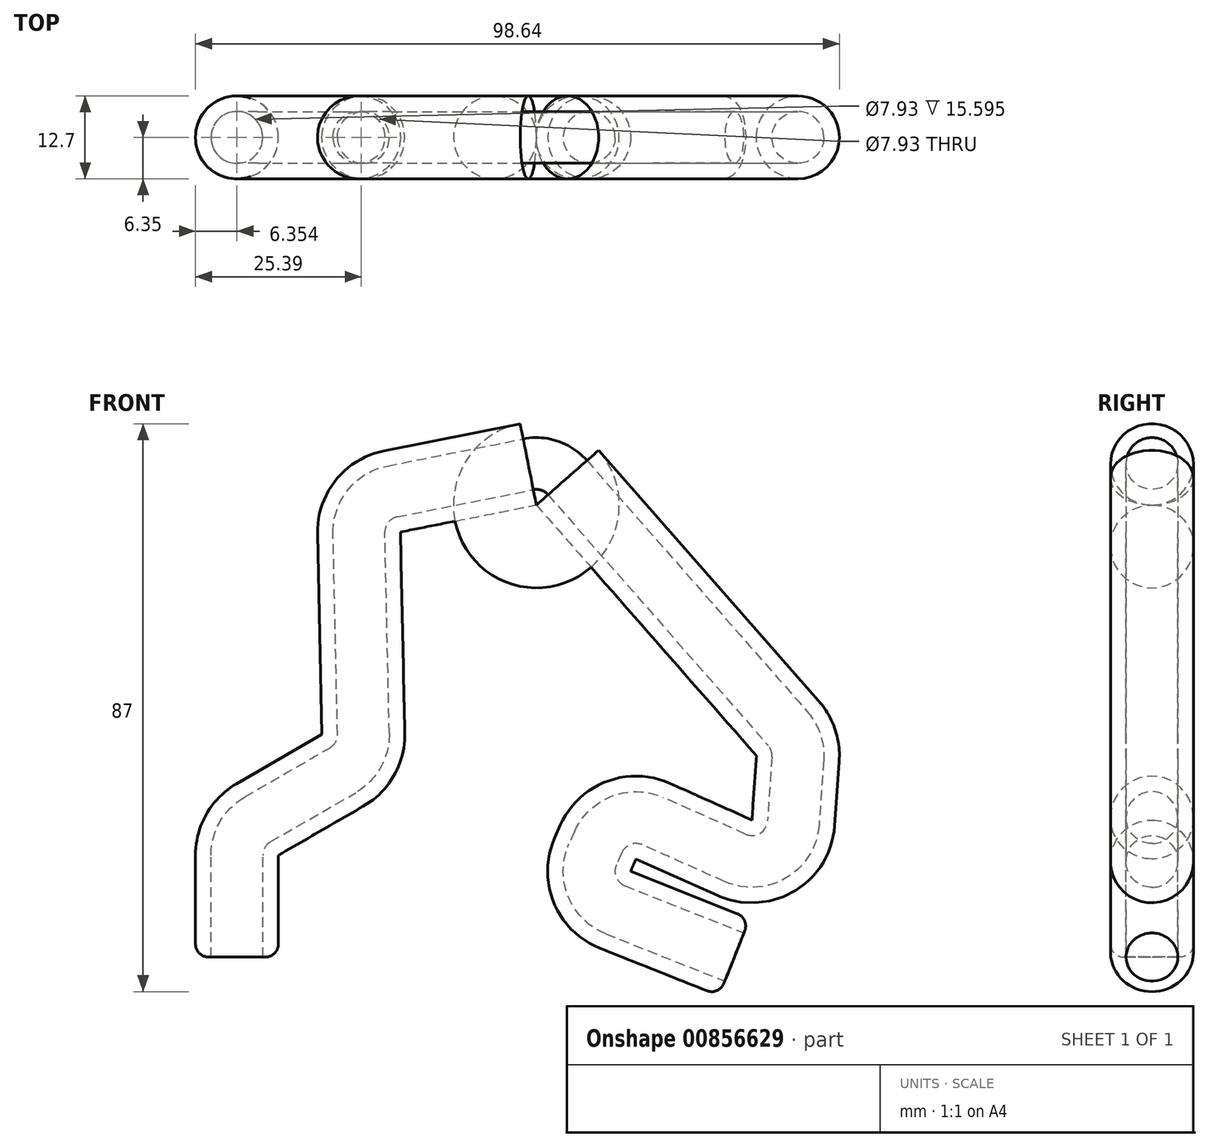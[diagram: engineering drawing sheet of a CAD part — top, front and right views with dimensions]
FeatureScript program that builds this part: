
annotation { "Feature Type Name" : "Feature", "Feature Type Description" : "" }
export const myFeature = defineFeature(function(context is Context, id is Id, definition is map)
    precondition{}
    {
        {
            var Q0;
            Q0=qCreatedBy(makeId("Front.planeOp"),FACE);
            var sketch = newSketch(context, id + "F0", { "sketchPlane" : qUnion([Q0])});
            skLineSegment(sketch, "E0", {"start": v(-44.89, 0) * mm, "end": v(-44.89, 15.6) * mm});
            skLineSegment(sketch, "E1", {"start": v(-41.71, 21.1) * mm, "end": v(-28.68, 28.62) * mm});
            skLineSegment(sketch, "E2", {"start": v(-25.5, 34.26) * mm, "end": v(-26.2, 64.96) * mm});
            skLineSegment(sketch, "E3", {"start": v(-21.08, 71.33) * mm, "end": v(-0.26, 75.48) * mm});
            skLineSegment(sketch, "E4", {"start": v(5.76, 73.44) * mm, "end": v(39.48, 35.03) * mm});
            skLineSegment(sketch, "E5", {"start": v(41.04, 30.39) * mm, "end": v(40.34, 20.56) * mm});
            skLineSegment(sketch, "E6", {"start": v(31.42, 15.2) * mm, "end": v(18.83, 20.82) * mm});
            skLineSegment(sketch, "E7", {"start": v(10.45, 17.61) * mm, "end": v(9.61, 15.75) * mm});
            skLineSegment(sketch, "E8", {"start": v(13.07, 7.26) * mm, "end": v(31.31, 0) * mm});
            skPoint(sketch, "E9.visualSharp", {"position": v(-44.89, 19.26) * mm});
            skArc(sketch, "E9.filletArc", {"start": v(-41.71, 21.1) * mm, "mid": v(-44.04, 18.77) * mm, "end": v(-44.89, 15.6) * mm});
            skPoint(sketch, "E10.visualSharp", {"position": v(-25.43, 30.5) * mm});
            skArc(sketch, "E10.filletArc", {"start": v(-28.68, 28.62) * mm, "mid": v(-26.32, 31) * mm, "end": v(-25.5, 34.26) * mm});
            skPoint(sketch, "E11.visualSharp", {"position": v(-26.3, 70.3) * mm});
            skArc(sketch, "E11.filletArc", {"start": v(-21.08, 71.33) * mm, "mid": v(-24.8, 69.08) * mm, "end": v(-26.2, 64.96) * mm});
            skPoint(sketch, "E12.visualSharp", {"position": v(3.34, 76.2) * mm});
            skArc(sketch, "E12.filletArc", {"start": v(5.76, 73.44) * mm, "mid": v(3.02, 75.27) * mm, "end": v(-0.26, 75.48) * mm});
            skPoint(sketch, "E13.visualSharp", {"position": v(41.23, 33.03) * mm});
            skArc(sketch, "E13.filletArc", {"start": v(41.04, 30.39) * mm, "mid": v(40.72, 32.86) * mm, "end": v(39.48, 35.03) * mm});
            skPoint(sketch, "E14.visualSharp", {"position": v(39.7, 11.5) * mm});
            skArc(sketch, "E14.filletArc", {"start": v(31.42, 15.2) * mm, "mid": v(37.27, 15.56) * mm, "end": v(40.34, 20.56) * mm});
            skPoint(sketch, "E15.visualSharp", {"position": v(13.03, 23.41) * mm});
            skArc(sketch, "E15.filletArc", {"start": v(18.83, 20.82) * mm, "mid": v(13.98, 20.96) * mm, "end": v(10.45, 17.61) * mm});
            skPoint(sketch, "E16.visualSharp", {"position": v(6.92, 9.7) * mm});
            skArc(sketch, "E16.filletArc", {"start": v(9.61, 15.75) * mm, "mid": v(9.53, 10.77) * mm, "end": v(13.07, 7.26) * mm});
            skSolve(sketch);
        }
        {
            var Q0;
            Q0=qCreatedBy(makeId("Top.planeOp"),FACE);
            var sketch = newSketch(context, id + "F1", { "sketchPlane" : qUnion([Q0])});
            skCircle(sketch, "E17", {"center": v(-44.89, 0) * mm, "radius": 6.35 * mm});
            skSolve(sketch);
        }
        {
            var Q0;
            Q0=makeQuery(id+"F1.imprint","IMPRINT",FACE,{"disambiguationData":[TD([[makeQuery(id+"F1.imprint","IMPRINT",EDGE,{"derivedFrom":sQuery(id+"F1.wireOp",EDGE,"E17")}),1.0]])]});
            var Q1;
            Q1 = qConstructionFilter(qBodyType(qCreatedBy(id + "F0" ,EDGE), BodyType.WIRE), ConstructionObject.NO);
            sweep(context, id + "F2", {"profiles" : qUnion([Q0]), "path" : qUnion([Q1])});
        }
        {
            var Q0;
            Q0=makeQuery(id+"F2.opSweep","CAP_FACE",FACE,{"disambiguationData":[OSD([sQuery(id+"F0.wireOp",VERTEX,"E0.start"),sQuery(id+"F1.wireOp",EDGE,"E17")])],"isStart":true});
            var sketch = newSketch(context, id + "F3", { "sketchPlane" : qUnion([Q0])});
            skCircle(sketch, "E18", {"center": v(-44.89, 0) * mm, "radius": 3.97 * mm});
            skSolve(sketch);
        }
        {
            var Q0;
            Q0=makeQuery(id+"F3.imprint","IMPRINT",FACE,{"disambiguationData":[TD([[makeQuery(id+"F3.imprint","IMPRINT",EDGE,{"derivedFrom":sQuery(id+"F3.wireOp",EDGE,"E18")}),1.0]])]});
            var Q1;
            Q1 = qConstructionFilter(qBodyType(qCreatedBy(id + "F0" ,EDGE), BodyType.WIRE), ConstructionObject.NO);
            sweep(context, id + "F4", {"operationType" : NewBodyOperationType.REMOVE, "profiles" : qUnion([Q0]), "path" : qUnion([Q1])});
        }
        {
            var Q0;
            Q0=makeQuery(id+"F2.opSweep","CAP_EDGE",EDGE,{"disambiguationData":[OSD([sQuery(id+"F0.wireOp",VERTEX,"E8.end"),sQuery(id+"F1.wireOp",EDGE,"E17")])],"isStart":false});
            var Q1;
            Q1=makeQuery(id+"F2.opSweep","CAP_EDGE",EDGE,{"disambiguationData":[OSD([sQuery(id+"F0.wireOp",VERTEX,"E0.start"),sQuery(id+"F1.wireOp",EDGE,"E17")])],"isStart":true});
            fillet(context, id + "F5", {"entities" : qUnion([Q0, Q1]), "radius" : 2.03 * mm, "tangentPropagation" : true, "allowEdgeOverflow" : false});
        }
    });
